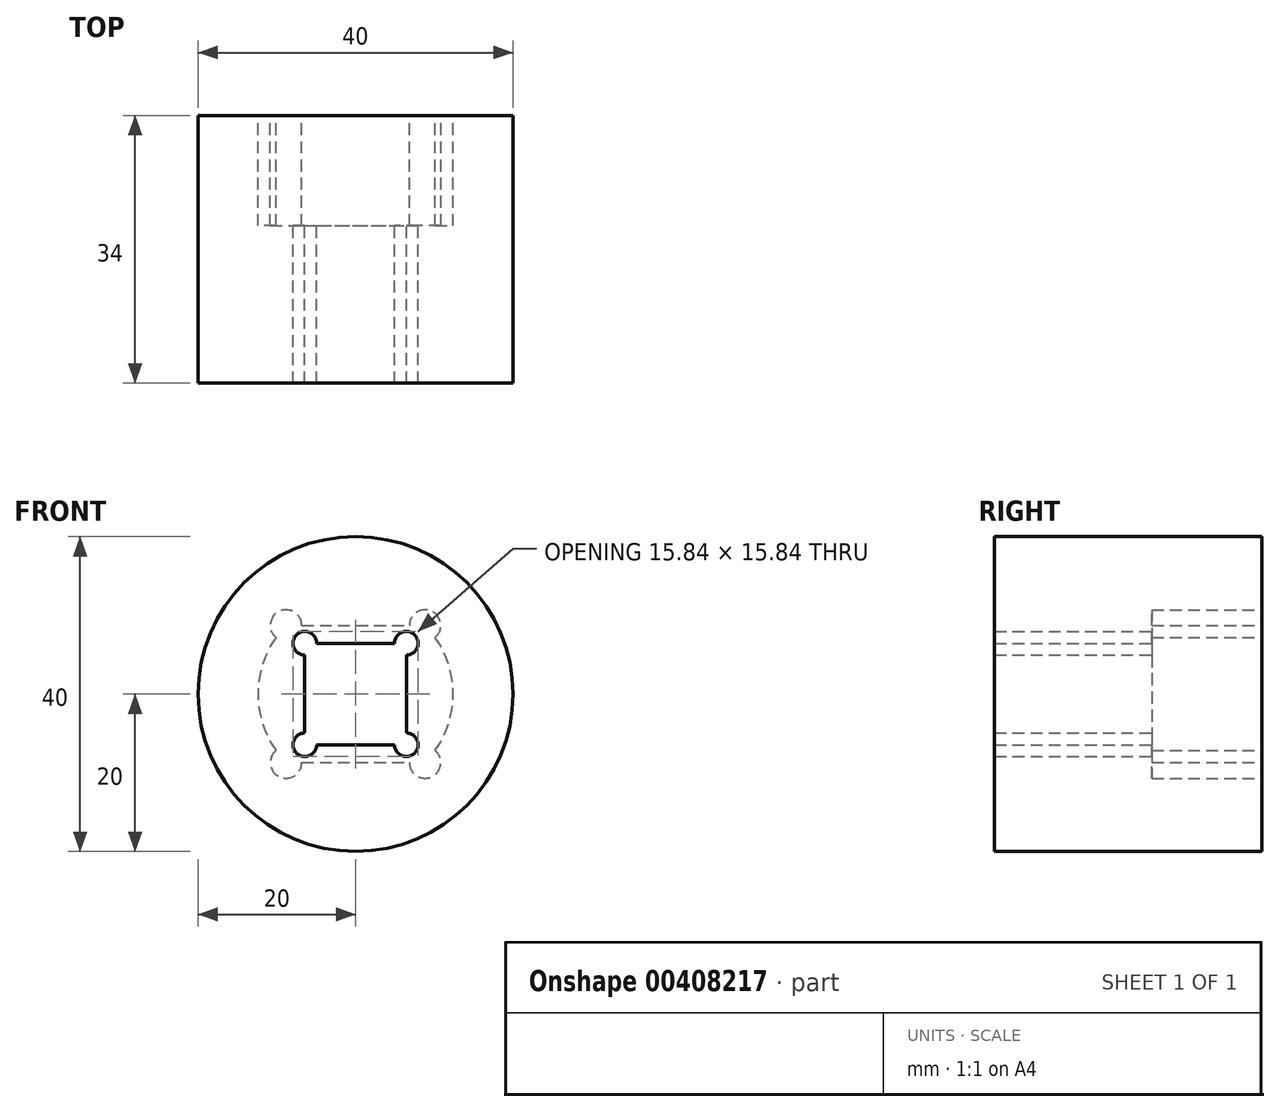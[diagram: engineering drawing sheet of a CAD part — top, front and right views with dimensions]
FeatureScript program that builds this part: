
annotation { "Feature Type Name" : "Feature", "Feature Type Description" : "" }
export const myFeature = defineFeature(function(context is Context, id is Id, definition is map)
    precondition{}
    {
        {
            var Q0;
            Q0=qCreatedBy(makeId("Front.planeOp"),FACE);
            var sketch = newSketch(context, id + "F0", { "sketchPlane" : qUnion([Q0])});
            skArc(sketch, "E0", {"start": v(-10.12, 7.17) * mm, "mid": v(-12.4, 0) * mm, "end": v(-10.12, -7.17) * mm});
            skLineSegment(sketch, "E1", {"start": v(-6.84, 8.7) * mm, "end": v(6.84, 8.7) * mm});
            skLineSegment(sketch, "E2", {"start": v(-6.84, -8.7) * mm, "end": v(6.84, -8.7) * mm});
            skArc(sketch, "E3.trimOffspring", {"start": v(10.12, -7.17) * mm, "mid": v(12.4, 0) * mm, "end": v(10.12, 7.17) * mm});
            skArc(sketch, "E4", {"start": v(-6.84, 8.7) * mm, "mid": v(-9.68, 10.51) * mm, "end": v(-10.12, 7.17) * mm});
            skArc(sketch, "E5", {"start": v(-10.12, -7.17) * mm, "mid": v(-9.68, -10.51) * mm, "end": v(-6.84, -8.7) * mm});
            skArc(sketch, "E6", {"start": v(6.84, -8.7) * mm, "mid": v(9.68, -10.51) * mm, "end": v(10.12, -7.17) * mm});
            skArc(sketch, "E7", {"start": v(10.12, 7.17) * mm, "mid": v(9.68, 10.51) * mm, "end": v(6.84, 8.7) * mm});
            skCircle(sketch, "E8", {"center": v(0, 0) * mm, "radius": 20 * mm});
            skSolve(sketch);
        }
        {
            var Q0;
            Q0 = qSketchRegion(id + "F0", true);
            extrude(context, id + "F1", {"entities" : qUnion([Q0]), "depth" : 14 * mm});
        }
        {
            var Q0;
            Q0=makeQuery(id+"F1.opExtrude","CAP_FACE",FACE,{"disambiguationData":[OSD([sQuery(id+"F0.wireOp",EDGE,"E0"),sQuery(id+"F0.wireOp",EDGE,"E1"),sQuery(id+"F0.wireOp",EDGE,"E2"),sQuery(id+"F0.wireOp",EDGE,"E3.trimOffspring"),sQuery(id+"F0.wireOp",EDGE,"E4"),sQuery(id+"F0.wireOp",EDGE,"E5"),sQuery(id+"F0.wireOp",EDGE,"E6"),sQuery(id+"F0.wireOp",EDGE,"E7"),sQuery(id+"F0.wireOp",EDGE,"E8")])],"isStart":false});
            var sketch = newSketch(context, id + "F2", { "sketchPlane" : qUnion([Q0])});
            skCircle(sketch, "E9", {"center": v(0, 0) * mm, "radius": 20 * mm});
            skLineSegment(sketch, "E10.bottom", {"start": v(-4.95, 6.45) * mm, "end": v(4.95, 6.45) * mm});
            skLineSegment(sketch, "E10.top", {"start": v(-4.95, -6.45) * mm, "end": v(4.95, -6.45) * mm});
            skLineSegment(sketch, "E10.left", {"start": v(-6.45, 4.95) * mm, "end": v(-6.45, -4.95) * mm});
            skLineSegment(sketch, "E10.right", {"start": v(6.45, 4.95) * mm, "end": v(6.45, -4.95) * mm});
            skArc(sketch, "E11", {"start": v(-4.95, 6.45) * mm, "mid": v(-7.51, 7.51) * mm, "end": v(-6.45, 4.95) * mm});
            skArc(sketch, "E12", {"start": v(-6.45, -4.95) * mm, "mid": v(-7.51, -7.51) * mm, "end": v(-4.95, -6.45) * mm});
            skArc(sketch, "E13", {"start": v(4.95, -6.45) * mm, "mid": v(7.51, -7.51) * mm, "end": v(6.45, -4.95) * mm});
            skArc(sketch, "E14", {"start": v(6.45, 4.95) * mm, "mid": v(7.51, 7.51) * mm, "end": v(4.95, 6.45) * mm});
            skSolve(sketch);
        }
        {
            var Q0;
            Q0 = qSketchRegion(id + "F2", true);
            extrude(context, id + "F3", {"entities" : qUnion([Q0]), "operationType" : NewBodyOperationType.ADD, "depth" : 20 * mm});
        }
    });
